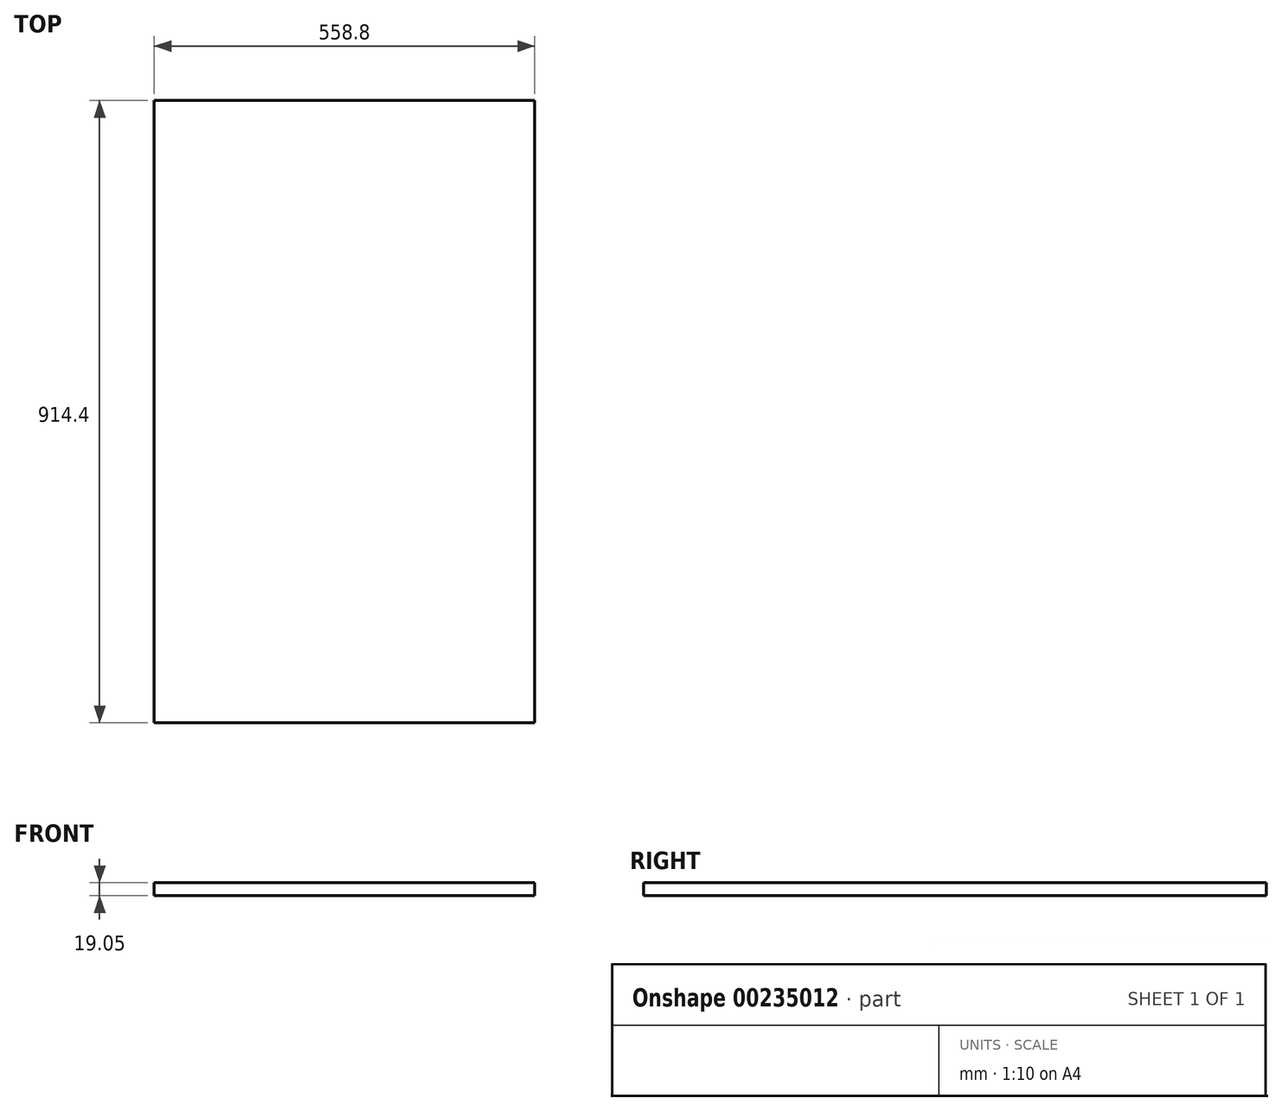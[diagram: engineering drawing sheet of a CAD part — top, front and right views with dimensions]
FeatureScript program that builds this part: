
annotation { "Feature Type Name" : "Feature", "Feature Type Description" : "" }
export const myFeature = defineFeature(function(context is Context, id is Id, definition is map)
    precondition{}
    {
        {
            var Q0;
            Q0=qCreatedBy(makeId("Top.planeOp"),FACE);
            var sketch = newSketch(context, id + "F0", { "sketchPlane" : qUnion([Q0])});
            skLineSegment(sketch, "E0.bottom", {"start": v(0, 457.2) * mm, "end": v(-558.8, 457.2) * mm});
            skLineSegment(sketch, "E0.top", {"start": v(0, -457.2) * mm, "end": v(-558.8, -457.2) * mm});
            skLineSegment(sketch, "E0.left", {"start": v(0, 457.2) * mm, "end": v(0, -457.2) * mm});
            skLineSegment(sketch, "E0.right", {"start": v(-558.8, 457.2) * mm, "end": v(-558.8, -457.2) * mm});
            skSolve(sketch);
        }
        {
            var Q0;
            Q0=makeQuery(id+"F0.imprint","IMPRINT",FACE,{"disambiguationData":[TD([[makeQuery(id+"F0.imprint","IMPRINT",EDGE,{"derivedFrom":sQuery(id+"F0.wireOp",EDGE,"E0.bottom")}),1.0]])]});
            extrude(context, id + "F1", {"entities" : qUnion([Q0]), "depth" : 19.05 * mm});
        }
    });
